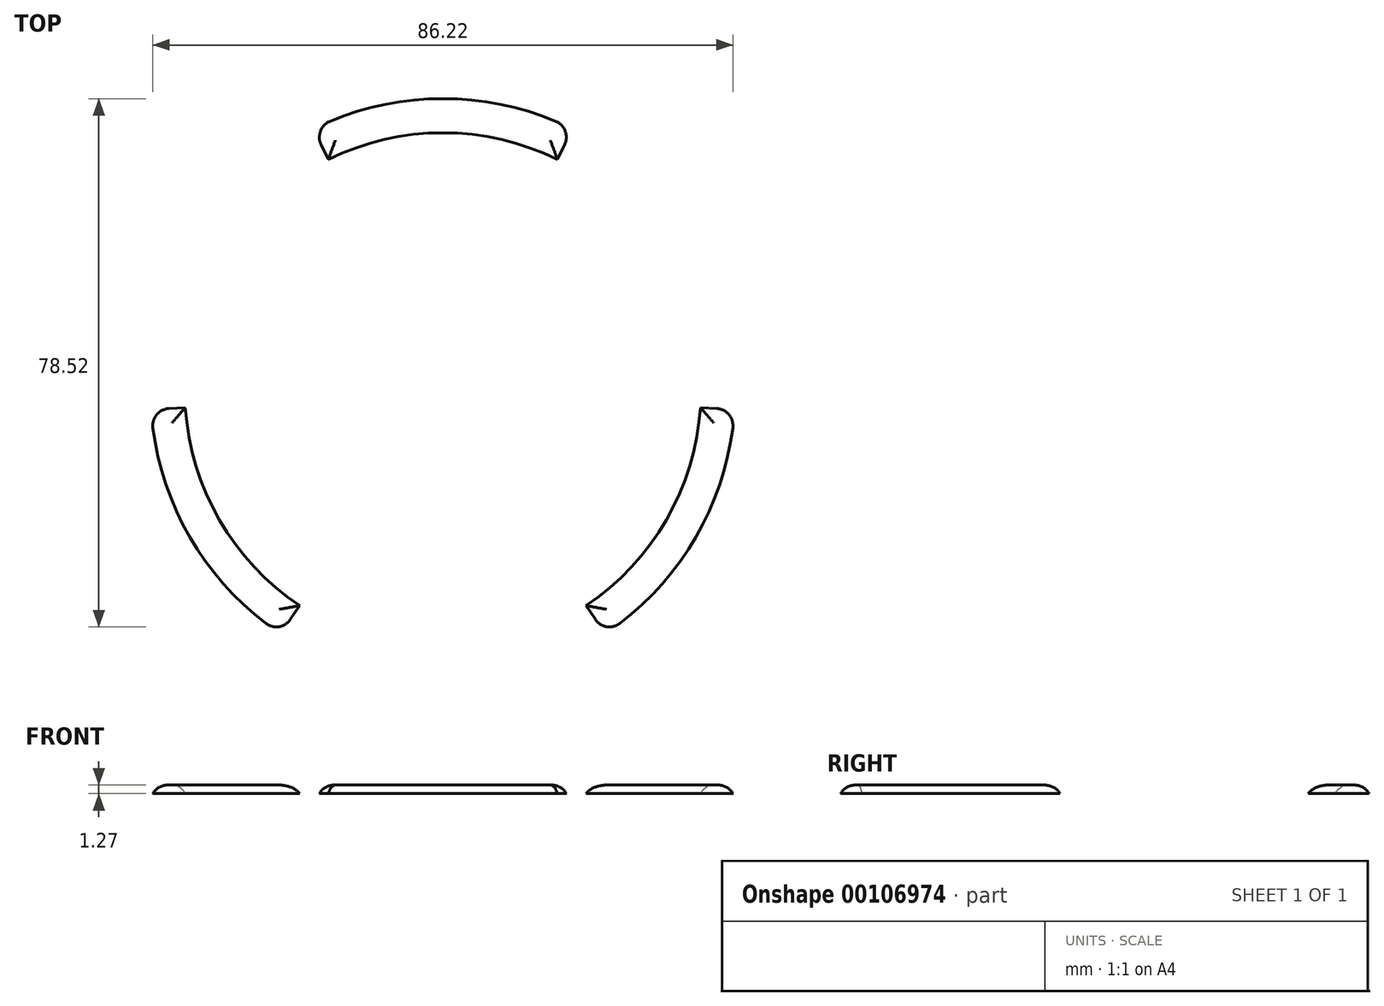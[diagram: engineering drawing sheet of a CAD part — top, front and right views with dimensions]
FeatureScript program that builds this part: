
annotation { "Feature Type Name" : "Feature", "Feature Type Description" : "" }
export const myFeature = defineFeature(function(context is Context, id is Id, definition is map)
    precondition{}
    {
        {
            var Q0;
            Q0=qCreatedBy(makeId("Top.planeOp"),FACE);
            var sketch = newSketch(context, id + "F0", { "sketchPlane" : qUnion([Q0])});
            skCircle(sketch, "E0", {"center": v(0, 0) * mm, "radius": 38.35 * mm});
            skCircle(sketch, "E1", {"center": v(0, 0) * mm, "radius": 43.43 * mm});
            skSolve(sketch);
        }
        {
            var Q0;
            Q0 = qSketchRegion(id + "F0", true);
            extrude(context, id + "F1", {"entities" : qUnion([Q0]), "depth" : 1.27 * mm});
        }
        {
            var Q0;
            Q0=qCreatedBy(makeId("Top.planeOp"),FACE);
            var sketch = newSketch(context, id + "F2", { "sketchPlane" : qUnion([Q0])});
            skLineSegment(sketch, "E2", {"start": v(0, 0) * mm, "end": v(-34.5, -51.73) * mm});
            skLineSegment(sketch, "E3", {"start": v(-34.5, -51.73) * mm, "end": v(0, -51.73) * mm});
            skLineSegment(sketch, "E4", {"start": v(0, 0) * mm, "end": v(0, -87.8) * mm, "construction": true});
            skLineSegment(sketch, "E5.MirrorCS", {"start": v(0, 0) * mm, "end": v(34.5, -51.73) * mm});
            skLineSegment(sketch, "E6.MirrorCS", {"start": v(34.5, -51.73) * mm, "end": v(0, -51.73) * mm});
            skLineSegment(sketch, "E7.1.0", {"start": v(0, 0) * mm, "end": v(62.05, -4.01) * mm});
            skLineSegment(sketch, "E7.1.1", {"start": v(0, 0) * mm, "end": v(27.55, 55.74) * mm});
            skLineSegment(sketch, "E7.1.2", {"start": v(27.55, 55.74) * mm, "end": v(44.8, 25.87) * mm});
            skLineSegment(sketch, "E7.1.3", {"start": v(62.05, -4.01) * mm, "end": v(44.8, 25.87) * mm});
            skLineSegment(sketch, "E7.2.0", {"start": v(0, 0) * mm, "end": v(-27.55, 55.74) * mm});
            skLineSegment(sketch, "E7.2.1", {"start": v(0, 0) * mm, "end": v(-62.05, -4.01) * mm});
            skLineSegment(sketch, "E7.2.2", {"start": v(-62.05, -4.01) * mm, "end": v(-44.8, 25.87) * mm});
            skLineSegment(sketch, "E7.2.3", {"start": v(-27.55, 55.74) * mm, "end": v(-44.8, 25.87) * mm});
            skPoint(sketch, "E7.center", {"position": v(0, 0) * mm});
            skSolve(sketch);
        }
        {
            var Q0;
            Q0 = qSketchRegion(id + "F2", true);
            extrude(context, id + "F3", {"entities" : qUnion([Q0]), "operationType" : NewBodyOperationType.REMOVE, "depth" : 25.4 * mm});
        }
        {
            var Q0;
            Q0=makeQuery(id+"F3.boolean.opBoolean","INTERSECT",EDGE,{"derivedFrom":[makeQuery(id+"F1.opExtrude","SWEPT_FACE",FACE,{"disambiguationData":[OSD([sQuery(id+"F0.wireOp",EDGE,"E1")])]}),makeQuery(id+"F3.opExtrude","SWEPT_FACE",FACE,{"disambiguationData":[OSD([sQuery(id+"F2.wireOp",EDGE,"E2")])]})]});
            var Q1;
            Q1=makeQuery(id+"F3.boolean.opBoolean","INTERSECT",EDGE,{"derivedFrom":[makeQuery(id+"F1.opExtrude","SWEPT_FACE",FACE,{"disambiguationData":[OSD([sQuery(id+"F0.wireOp",EDGE,"E1")])]}),makeQuery(id+"F3.opExtrude","SWEPT_FACE",FACE,{"disambiguationData":[OSD([sQuery(id+"F2.wireOp",EDGE,"E5.MirrorCS")])]})]});
            var Q2;
            Q2=makeQuery(id+"F3.boolean.opBoolean","INTERSECT",EDGE,{"derivedFrom":[makeQuery(id+"F1.opExtrude","SWEPT_FACE",FACE,{"disambiguationData":[OSD([sQuery(id+"F0.wireOp",EDGE,"E1")])]}),makeQuery(id+"F3.opExtrude","SWEPT_FACE",FACE,{"disambiguationData":[OSD([sQuery(id+"F2.wireOp",EDGE,"E7.2.1")])]})]});
            var Q3;
            Q3=makeQuery(id+"F3.boolean.opBoolean","INTERSECT",EDGE,{"derivedFrom":[makeQuery(id+"F1.opExtrude","SWEPT_FACE",FACE,{"disambiguationData":[OSD([sQuery(id+"F0.wireOp",EDGE,"E1")])]}),makeQuery(id+"F3.opExtrude","SWEPT_FACE",FACE,{"disambiguationData":[OSD([sQuery(id+"F2.wireOp",EDGE,"E7.1.0")])]})]});
            var Q4;
            Q4=makeQuery(id+"F3.boolean.opBoolean","INTERSECT",EDGE,{"derivedFrom":[makeQuery(id+"F1.opExtrude","SWEPT_FACE",FACE,{"disambiguationData":[OSD([sQuery(id+"F0.wireOp",EDGE,"E1")])]}),makeQuery(id+"F3.opExtrude","SWEPT_FACE",FACE,{"disambiguationData":[OSD([sQuery(id+"F2.wireOp",EDGE,"E7.1.1")])]})]});
            var Q5;
            Q5=makeQuery(id+"F3.boolean.opBoolean","INTERSECT",EDGE,{"derivedFrom":[makeQuery(id+"F1.opExtrude","SWEPT_FACE",FACE,{"disambiguationData":[OSD([sQuery(id+"F0.wireOp",EDGE,"E1")])]}),makeQuery(id+"F3.opExtrude","SWEPT_FACE",FACE,{"disambiguationData":[OSD([sQuery(id+"F2.wireOp",EDGE,"E7.2.0")])]})]});
            fillet(context, id + "F4", {"entities" : qUnion([Q0, Q1, Q2, Q3, Q4, Q5]), "radius" : 2.54 * mm, "tangentPropagation" : true, "allowEdgeOverflow" : false});
        }
        {
            var Q0;
            {var subQ0=sQuery(id+"F0.wireOp",EDGE,"E1");Q0=makeQuery(id+"F3.boolean.opBoolean","SPLIT",EDGE,{"disambiguationData":[TD([makeQuery(id+"F3.opExtrude","SWEPT_FACE",FACE,{"disambiguationData":[OSD([sQuery(id+"F2.wireOp",EDGE,"E5.MirrorCS")])]})])],"derivedFrom":makeQuery(id+"F1.opExtrude","CAP_EDGE",EDGE,{"disambiguationData":[OSD([subQ0])],"isStart":false})});}
            var Q1;
            {var subQ0=sQuery(id+"F0.wireOp",EDGE,"E1");Q1=makeQuery(id+"F3.boolean.opBoolean","SPLIT",EDGE,{"disambiguationData":[TD([makeQuery(id+"F3.opExtrude","SWEPT_FACE",FACE,{"disambiguationData":[OSD([sQuery(id+"F2.wireOp",EDGE,"E7.1.1")])]})])],"derivedFrom":makeQuery(id+"F1.opExtrude","CAP_EDGE",EDGE,{"disambiguationData":[OSD([subQ0])],"isStart":false})});}
            var Q2;
            {var subQ0=sQuery(id+"F0.wireOp",EDGE,"E1");Q2=makeQuery(id+"F3.boolean.opBoolean","SPLIT",EDGE,{"disambiguationData":[TD([makeQuery(id+"F3.opExtrude","SWEPT_FACE",FACE,{"disambiguationData":[OSD([sQuery(id+"F2.wireOp",EDGE,"E2")])]})])],"derivedFrom":makeQuery(id+"F1.opExtrude","CAP_EDGE",EDGE,{"disambiguationData":[OSD([subQ0])],"isStart":false})});}
            var Q3;
            {var subQ0=sQuery(id+"F0.wireOp",EDGE,"E0");Q3=makeQuery(id+"F3.boolean.opBoolean","SPLIT",EDGE,{"disambiguationData":[TD([makeQuery(id+"F3.opExtrude","SWEPT_FACE",FACE,{"disambiguationData":[OSD([sQuery(id+"F2.wireOp",EDGE,"E5.MirrorCS")])]})])],"derivedFrom":makeQuery(id+"F1.opExtrude","CAP_EDGE",EDGE,{"disambiguationData":[OSD([subQ0])],"isStart":false})});}
            var Q4;
            {var subQ0=sQuery(id+"F0.wireOp",EDGE,"E0");Q4=makeQuery(id+"F3.boolean.opBoolean","SPLIT",EDGE,{"disambiguationData":[TD([makeQuery(id+"F3.opExtrude","SWEPT_FACE",FACE,{"disambiguationData":[OSD([sQuery(id+"F2.wireOp",EDGE,"E2")])]})])],"derivedFrom":makeQuery(id+"F1.opExtrude","CAP_EDGE",EDGE,{"disambiguationData":[OSD([subQ0])],"isStart":false})});}
            var Q5;
            {var subQ0=sQuery(id+"F0.wireOp",EDGE,"E0");Q5=makeQuery(id+"F3.boolean.opBoolean","SPLIT",EDGE,{"disambiguationData":[TD([makeQuery(id+"F3.opExtrude","SWEPT_FACE",FACE,{"disambiguationData":[OSD([sQuery(id+"F2.wireOp",EDGE,"E7.1.1")])]})])],"derivedFrom":makeQuery(id+"F1.opExtrude","CAP_EDGE",EDGE,{"disambiguationData":[OSD([subQ0])],"isStart":false})});}
            fillet(context, id + "F5", {"entities" : qUnion([Q0, Q1, Q2, Q3, Q4, Q5]), "radius" : 2.54 * mm, "tangentPropagation" : true, "allowEdgeOverflow" : false});
        }
    });
